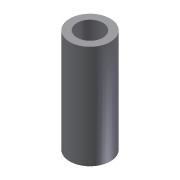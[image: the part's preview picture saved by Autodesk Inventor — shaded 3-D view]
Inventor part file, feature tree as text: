
AUTODESK INVENTOR PART (.ipt)
format: ipt  version: 2012 (Build 160160000, 160)  size: 72,704 bytes
history: native  units: mm
features: extrude x1, sketch x1
ambient origin geometry x8: Origin, YZ Plane, XZ Plane, XY Plane, X Axis, Y Axis, Z Axis, Center Point
bodies: Solid1 (feature_tree)
feature tree (2):
  extrude  "Extrusion1"  Depth=5.1mm
  sketch  "Sketch1"  dims[d0=8.0mm d1=5.1mm d2=20.4mm d3=0.0mm]
